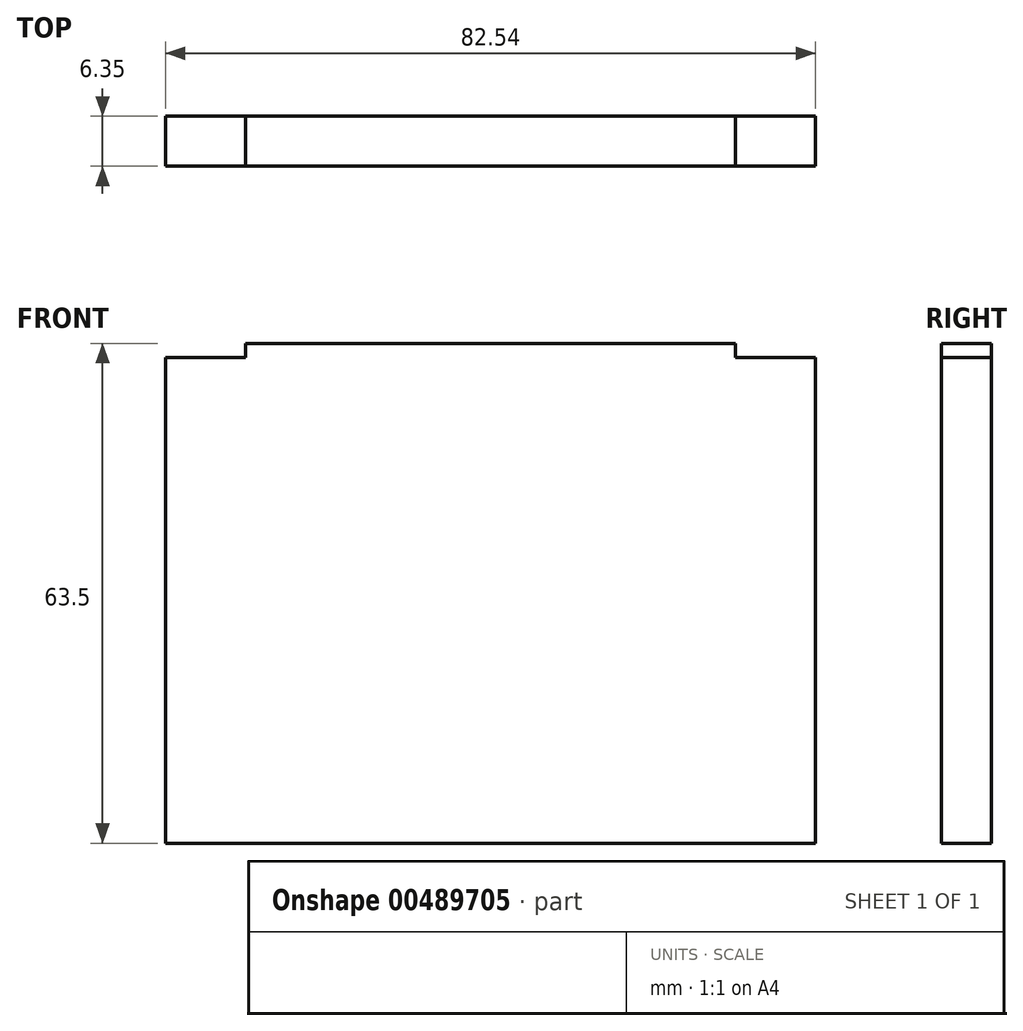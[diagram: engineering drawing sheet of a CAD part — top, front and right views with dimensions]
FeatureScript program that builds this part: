
annotation { "Feature Type Name" : "Feature", "Feature Type Description" : "" }
export const myFeature = defineFeature(function(context is Context, id is Id, definition is map)
    precondition{}
    {
        {
            var Q0;
            Q0=qCreatedBy(makeId("Front.planeOp"),FACE);
            var sketch = newSketch(context, id + "F0", { "sketchPlane" : qUnion([Q0])});
            skLineSegment(sketch, "E0.bottom", {"start": v(31.12, 31.75) * mm, "end": v(-31.12, 31.75) * mm});
            skLineSegment(sketch, "E0.top", {"start": v(41.28, -31.75) * mm, "end": v(-41.28, -31.75) * mm});
            skLineSegment(sketch, "E0.left", {"start": v(41.28, 29.97) * mm, "end": v(41.28, -31.75) * mm});
            skLineSegment(sketch, "E0.right", {"start": v(-41.28, 31.75) * mm, "end": v(-41.27, -31.75) * mm});
            skPoint(sketch, "E0.middle", {"position": v(0, 0) * mm});
            skLineSegment(sketch, "E1.top", {"start": v(-41.28, 29.97) * mm, "end": v(-31.12, 29.97) * mm});
            skLineSegment(sketch, "E1.right", {"start": v(-31.12, 31.75) * mm, "end": v(-31.12, 29.97) * mm});
            skLineSegment(sketch, "E2.MirrorCS", {"start": v(41.28, 29.97) * mm, "end": v(31.12, 29.97) * mm});
            skLineSegment(sketch, "E3.MirrorCS", {"start": v(31.12, 31.75) * mm, "end": v(31.12, 29.97) * mm});
            skPoint(sketch, "E4.orphan", {"position": v(41.28, 31.75) * mm});
            skSolve(sketch);
        }
        {
            var Q0;
            Q0 = qSketchRegion(id + "F0", true);
            extrude(context, id + "F1", {"entities" : qUnion([Q0]), "depth" : 6.35 * mm});
        }
    });
